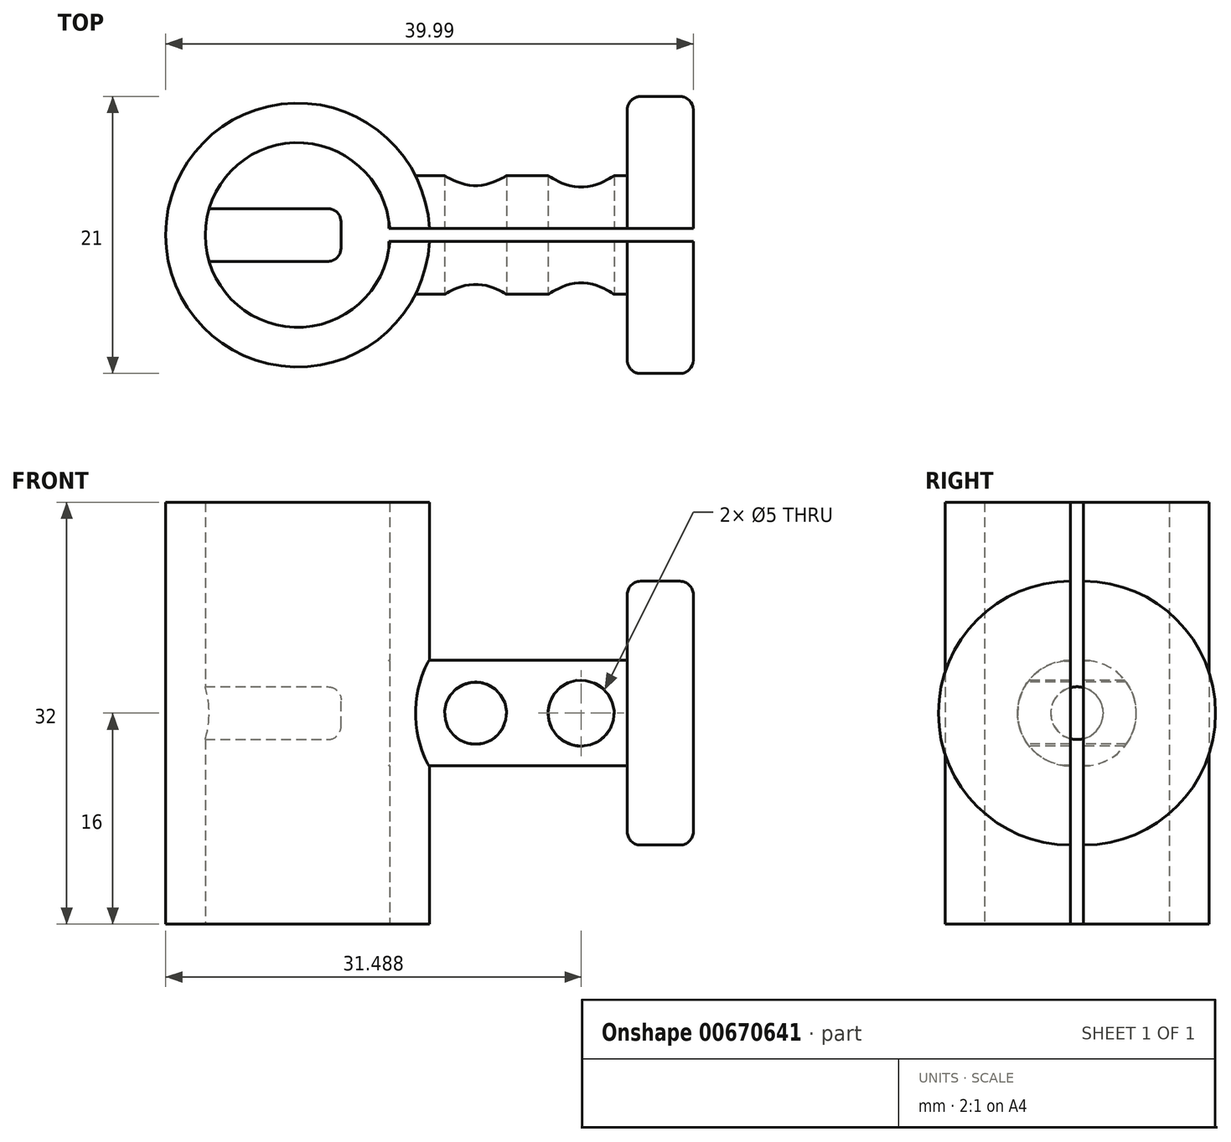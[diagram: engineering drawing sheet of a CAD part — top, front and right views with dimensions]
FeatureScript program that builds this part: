
annotation { "Feature Type Name" : "Feature", "Feature Type Description" : "" }
export const myFeature = defineFeature(function(context is Context, id is Id, definition is map)
    precondition{}
    {
        {
            var Q0;
            Q0=qCreatedBy(makeId("Top.planeOp"),FACE);
            var sketch = newSketch(context, id + "F0", { "sketchPlane" : qUnion([Q0])});
            skCircle(sketch, "E0", {"center": v(0, 0) * mm, "radius": 7 * mm});
            skCircle(sketch, "E1.0", {"center": v(0, 0) * mm, "radius": 10 * mm});
            skLineSegment(sketch, "E2", {"start": v(9.99, 0.5) * mm, "end": v(24.99, 0.5) * mm});
            skLineSegment(sketch, "E3", {"start": v(24.99, 0.5) * mm, "end": v(24.99, 9.5) * mm});
            skLineSegment(sketch, "E4", {"start": v(25.99, 10.5) * mm, "end": v(28.99, 10.5) * mm});
            skLineSegment(sketch, "E5", {"start": v(29.99, 9.5) * mm, "end": v(29.99, 0.5) * mm});
            skLineSegment(sketch, "E6", {"start": v(29.99, 0.5) * mm, "end": v(24.99, 0.5) * mm});
            skLineSegment(sketch, "E7", {"start": v(8.93, 4.5) * mm, "end": v(24.99, 4.5) * mm});
            skLineSegment(sketch, "E8", {"start": v(-6.7, 2) * mm, "end": v(2.3, 2) * mm});
            skLineSegment(sketch, "E9", {"start": v(3.3, 1) * mm, "end": v(3.3, 0) * mm});
            skLineSegment(sketch, "E10", {"start": v(3.3, 0) * mm, "end": v(-10, 0) * mm});
            skPoint(sketch, "E11.visualSharp", {"position": v(29.99, 10.5) * mm});
            skArc(sketch, "E11.filletArc", {"start": v(29.99, 9.5) * mm, "mid": v(29.7, 10.2) * mm, "end": v(28.99, 10.5) * mm});
            skPoint(sketch, "E12.visualSharp", {"position": v(24.99, 10.5) * mm});
            skArc(sketch, "E12.filletArc", {"start": v(25.99, 10.5) * mm, "mid": v(25.28, 10.2) * mm, "end": v(24.99, 9.5) * mm});
            skPoint(sketch, "E13.visualSharp", {"position": v(3.3, 2) * mm});
            skArc(sketch, "E13.filletArc", {"start": v(3.3, 1) * mm, "mid": v(3, 1.7) * mm, "end": v(2.3, 2) * mm});
            skLineSegment(sketch, "E14", {"start": v(9.99, 0.5) * mm, "end": v(6.98, 0.5) * mm});
            skLineSegment(sketch, "E15.MirrorCS", {"start": v(9.99, -0.5) * mm, "end": v(6.98, -0.5) * mm});
            skLineSegment(sketch, "E16.MirrorCS", {"start": v(9.99, -0.5) * mm, "end": v(24.99, -0.5) * mm});
            skLineSegment(sketch, "E17.MirrorCS", {"start": v(29.99, -0.5) * mm, "end": v(24.99, -0.5) * mm});
            skLineSegment(sketch, "E18.MirrorCS", {"start": v(29.99, -9.5) * mm, "end": v(29.99, -0.5) * mm});
            skArc(sketch, "E19.MirrorCS", {"start": v(29.99, -9.5) * mm, "mid": v(29.7, -10.2) * mm, "end": v(28.99, -10.5) * mm});
            skLineSegment(sketch, "E20.MirrorCS", {"start": v(25.99, -10.5) * mm, "end": v(28.99, -10.5) * mm});
            skArc(sketch, "E21.MirrorCS", {"start": v(25.99, -10.5) * mm, "mid": v(25.28, -10.2) * mm, "end": v(24.99, -9.5) * mm});
            skLineSegment(sketch, "E22.MirrorCS", {"start": v(24.99, -0.5) * mm, "end": v(24.99, -9.5) * mm});
            skLineSegment(sketch, "E23.MirrorCS", {"start": v(8.93, -4.5) * mm, "end": v(24.99, -4.5) * mm});
            skLineSegment(sketch, "E24", {"start": v(-6.7, 2) * mm, "end": v(-9.8, 2) * mm});
            skLineSegment(sketch, "E25", {"start": v(8.93, 4.5) * mm, "end": v(6.93, 4.5) * mm});
            skLineSegment(sketch, "E26.MirrorCS", {"start": v(8.93, -4.5) * mm, "end": v(6.93, -4.5) * mm});
            skArc(sketch, "E27", {"start": v(6.98, 0.5) * mm, "mid": v(7.72, 2.51) * mm, "end": v(6.93, 4.5) * mm});
            skArc(sketch, "E28.MirrorCS", {"start": v(6.98, -0.5) * mm, "mid": v(7.72, -2.51) * mm, "end": v(6.93, -4.5) * mm});
            skSolve(sketch);
        }
        {
            var Q0;
            {var subQ0=sQuery(id+"F0.wireOp",EDGE,"E14");Q0=makeQuery(id+"F0.imprint","IMPRINT",FACE,{"disambiguationData":[TD([[makeQuery(id+"F0.imprint","IMPRINT",EDGE,{"derivedFrom":subQ0}),-1.0]])]});}
            var Q1;
            {var subQ0=sQuery(id+"F0.wireOp",EDGE,"E24");Q1=makeQuery(id+"F0.imprint","IMPRINT",FACE,{"disambiguationData":[TD([[makeQuery(id+"F0.imprint","IMPRINT",EDGE,{"derivedFrom":subQ0}),1.0]])]});}
            var Q2;
            {var subQ5=sQuery(id+"F0.wireOp",EDGE,"E15.MirrorCS");Q2=makeQuery(id+"F0.imprint","IMPRINT",FACE,{"disambiguationData":[TD([[makeQuery(id+"F0.imprint","IMPRINT",EDGE,{"derivedFrom":subQ5}),1.0]])]});}
            var Q3;
            {var subQ0=sQuery(id+"F0.wireOp",EDGE,"E26.MirrorCS");Q3=makeQuery(id+"F0.imprint","IMPRINT",FACE,{"disambiguationData":[TD([[makeQuery(id+"F0.imprint","IMPRINT",EDGE,{"derivedFrom":subQ0}),1.0]])]});}
            var Q4;
            {var subQ0=sQuery(id+"F0.wireOp",EDGE,"E24");Q4=makeQuery(id+"F0.imprint","IMPRINT",FACE,{"disambiguationData":[TD([[makeQuery(id+"F0.imprint","IMPRINT",EDGE,{"derivedFrom":subQ0}),-1.0]])]});}
            extrude(context, id + "F1", {"entities" : qUnion([Q0, Q1, Q2, Q3, Q4]), "endBound" : BoundingType.SYMMETRIC, "depth" : 32 * mm, "offsetDistance" : 25 * mm});
        }
        {
            var Q0;
            {var subQ0=sQuery(id+"F0.wireOp",EDGE,"E24");Q0=makeQuery(id+"F0.imprint","IMPRINT",FACE,{"disambiguationData":[TD([[makeQuery(id+"F0.imprint","IMPRINT",EDGE,{"derivedFrom":subQ0}),1.0]])]});}
            var Q1;
            {var subQ4=sQuery(id+"F0.wireOp",EDGE,"E8");Q1=makeQuery(id+"F0.imprint","IMPRINT",FACE,{"disambiguationData":[TD([[makeQuery(id+"F0.imprint","IMPRINT",EDGE,{"derivedFrom":subQ4}),-1.0]])]});}
            var Q2;
            Q2=sQuery(id+"F0.wireOp",EDGE,"E10");
            revolve(context, id + "F2", {"operationType" : NewBodyOperationType.ADD, "entities" : qUnion([Q0, Q1]), "axis" : qUnion([Q2]), "revolveType" : RevolveType.FULL});
        }
        {
            var Q0;
            {var subQ0=sQuery(id+"F0.wireOp",EDGE,"E14");Q0=makeQuery(id+"F0.imprint","IMPRINT",FACE,{"disambiguationData":[TD([[makeQuery(id+"F0.imprint","IMPRINT",EDGE,{"derivedFrom":subQ0}),-1.0]])]});}
            var Q1;
            {var subQ0=sQuery(id+"F0.wireOp",EDGE,"E2");Q1=makeQuery(id+"F0.imprint","IMPRINT",FACE,{"disambiguationData":[TD([[makeQuery(id+"F0.imprint","IMPRINT",EDGE,{"derivedFrom":subQ0}),1.0]])]});}
            var Q2;
            Q2=makeQuery(id+"F0.imprint","IMPRINT",FACE,{"disambiguationData":[TD([[makeQuery(id+"F0.imprint","IMPRINT",EDGE,{"derivedFrom":sQuery(id+"F0.wireOp",EDGE,"E4")}),-1.0]])]});
            var Q3;
            Q3=sQuery(id+"F0.wireOp",EDGE,"E2");
            revolve(context, id + "F3", {"operationType" : NewBodyOperationType.ADD, "entities" : qUnion([Q0, Q1, Q2]), "axis" : qUnion([Q3]), "revolveType" : RevolveType.SYMMETRIC, "angle" : 180 * degree});
        }
        {
            var Q0;
            {var subQ0=sQuery(id+"F0.wireOp",EDGE,"E16.MirrorCS");Q0=makeQuery(id+"F0.imprint","IMPRINT",FACE,{"disambiguationData":[TD([[makeQuery(id+"F0.imprint","IMPRINT",EDGE,{"derivedFrom":subQ0}),-1.0]])]});}
            var Q1;
            {var subQ0=sQuery(id+"F0.wireOp",EDGE,"E17.MirrorCS");Q1=makeQuery(id+"F0.imprint","IMPRINT",FACE,{"disambiguationData":[TD([[makeQuery(id+"F0.imprint","IMPRINT",EDGE,{"derivedFrom":subQ0}),1.0]])]});}
            var Q2;
            {var subQ0=sQuery(id+"F0.wireOp",EDGE,"E15.MirrorCS");Q2=makeQuery(id+"F0.imprint","IMPRINT",FACE,{"disambiguationData":[TD([[makeQuery(id+"F0.imprint","IMPRINT",EDGE,{"derivedFrom":subQ0}),1.0]])]});}
            var Q3;
            Q3=sQuery(id+"F0.wireOp",EDGE,"E16.MirrorCS");
            revolve(context, id + "F4", {"operationType" : NewBodyOperationType.ADD, "entities" : qUnion([Q0, Q1, Q2]), "axis" : qUnion([Q3]), "revolveType" : RevolveType.SYMMETRIC, "angle" : 180 * degree});
        }
        {
            var Q0;
            Q0=qCreatedBy(makeId("Front.planeOp"),FACE);
            var sketch = newSketch(context, id + "F5", { "sketchPlane" : qUnion([Q0])});
            skCircle(sketch, "E29", {"center": v(13.49, 0) * mm, "radius": 2.35 * mm});
            skCircle(sketch, "E30", {"center": v(21.49, 0) * mm, "radius": 2.5 * mm});
            skLineSegment(sketch, "E31", {"start": v(13.49, 0) * mm, "end": v(21.49, 0) * mm, "construction": true});
            skSolve(sketch);
        }
        {
            var Q0;
            Q0=makeQuery(id+"F5.imprint","IMPRINT",FACE,{"disambiguationData":[TD([[makeQuery(id+"F5.imprint","IMPRINT",EDGE,{"derivedFrom":sQuery(id+"F5.wireOp",EDGE,"E29")}),1.0]])]});
            var Q1;
            Q1=makeQuery(id+"F5.imprint","IMPRINT",FACE,{"disambiguationData":[TD([[makeQuery(id+"F5.imprint","IMPRINT",EDGE,{"derivedFrom":sQuery(id+"F5.wireOp",EDGE,"E30")}),1.0]])]});
            extrude(context, id + "F6", {"entities" : qUnion([Q0, Q1]), "operationType" : NewBodyOperationType.REMOVE, "endBound" : BoundingType.SYMMETRIC, "oppositeDirection" : true, "depth" : 40 * mm, "offsetDistance" : 25 * mm});
        }
    });
